# Revit family: Hager-GOLF-Surface_mounted-IP40-With_Cover-With_DIN-Hosted-ES-es
name_source: partatom
category: Electrical Equipment
units: mm (PartAtom-declared; Revit-internal decimal feet)

## family parameters
Cut with Voids When Loaded = No
Host = Face
Maintain Annotation Orientation = Yes
Panel Configuration = Two Columns, Circuits Across
Part Type = Panelboard
Room Calculation Point = No
Round Connector Dimension = Use Diameter
Shared = No

## types (38) — shared parameters
BC_MODEL_ID = 1539134
BC_OBJECT_ID = 512269
BC_OBJECT_VERSION = #5
Code hager = ADD-EC000214_EU
EF000003 - Método de montaje = Montado superficial (escayola)
EF000007 - Color = Blanco
EF000024 - Resistente a UV = No
EF000049 - Profundidad = 99 mm  [stored 0.324803 ft]
EF000116 - Número RAL = 9010
EF000118 - Con placa de montaje = No
EF001062 - Versión de CEM = No
EF001088 - Posibilidad de extensión = Yes
EF001134 - Carril DIN = Yes
EF004462 - Tipo de cierre = Otros
EF005474 - Grado de protección (IP) = IP40
EF006306 - Con candado = No
EF009212 - Versión de la cubierta = Cerrado
EF015941 - Puerta de transmisión de señal = Yes
ETIM class code = EC000214
ETIM class name = Small distribution board
HG000001 - Número de columnas = 1
HG000002-with door or cover-es = Yes
HG000003-Range-es = GOLF
HG000005-Thickness-es = 2 mm  [stored 0.00656168 ft]
HG000006-Flush mounted-es = No
HG000009-Double swing door-es = No
HG000010-Asymmetric doors-es = No
HG000011-Empty rows from bottom-es = No
HG000012-Door swing angle-es = 90.00°
HG000013-Door on the left-es = No
HG000014-Door on the right-es = Yes
HG000015-Clearance visibility-es = Yes
HG000016-Door 3D visibility-es = Yes
HG000017-Distance between poles-es = 18 mm  [stored 0.0590551 ft]
HG000060-RAL-number = 9010
HG000099-Onfly Template ID-es-ES = 507532
Manufacturer = Hager
Name = Hager-GOLF-Surface_mounted-IP40-With_Cover-With_DIN-NoHosted-ES-es
Name BIM&CO = Electricity
Name hager = ADD_Enclosures_EC000214
Uniformat = Low Tension Service & Dist.
Uniformat code = D501001
zero-valued in all types: Default Elevation, EF000218 - Profundidad de instalación, EF000332 - Altura de la instalación, EF000846 - Anchura de montaje, EF001131 - Profundidad interna, HG000007-Number of empty columns-es, HG000008-Number of empty rows-es

## per-type parameters (varying)
| type | BC_VARIANT_ID | EF000008 - Anchura | EF000040 - Altura | EF000266 - Número de filas | EF002950 - Ancho en número de espacios modulares | EF006244 - Tapa/puerta transparente | EF015776 - Borne de tierra | EF015777 - Borne neutro | HG000004-Manufacturer reference-es | HGEF000266-Número de filas | HGEF0002950-Ancho en número de espacios modulares |
| GOLF-Surface_mounted_W138_H184_D99_4_Modular_Spacing-VS104PE | 1169241 | 138 mm  [stored 0.452756 ft] | 184 mm  [stored 0.603675 ft] | 1 | 4 | No | Yes | No | VS104PE | 1 | 4 |
| GOLF-Surface_mounted_W138_H184_D99_4_Modular_Spacing-VS104PEB | 1169246 | 138 mm  [stored 0.452756 ft] | 184 mm  [stored 0.603675 ft] | 1 | 4 | No | No | No | VS104PEB | 1 | 4 |
| GOLF-Surface_mounted_W138_H184_D99_4_Modular_Spacing-VS104TE | 1169249 | 138 mm  [stored 0.452756 ft] | 184 mm  [stored 0.603675 ft] | 1 | 4 | Yes | Yes | No | VS104TE | 1 | 4 |
| GOLF-Surface_mounted_W210_H184_D99_8_Modular_Spacing-VS108PE | 1169253 | 210 mm  [stored 0.688976 ft] | 184 mm  [stored 0.603675 ft] | 1 | 8 | No | Yes | No | VS108PE | 1 | 8 |
| GOLF-Surface_mounted_W210_H184_D99_8_Modular_Spacing-VS108PEB | 1169256 | 210 mm  [stored 0.688976 ft] | 184 mm  [stored 0.603675 ft] | 1 | 8 | No | No | No | VS108PEB | 1 | 8 |
| GOLF-Surface_mounted_W210_H184_D99_8_Modular_Spacing-VS108TE | 1169260 | 210 mm  [stored 0.688976 ft] | 184 mm  [stored 0.603675 ft] | 1 | 8 | Yes | Yes | No | VS108TE | 1 | 8 |
| GOLF-Surface_mounted_W282_H252_D99_12_Modular_Spacing-VS112PE | 1169262 | 282 mm | 252 mm  [stored 0.826772 ft] | 1 | 12 | No | Yes | No | VS112PE | 1 | 12 |
| GOLF-Surface_mounted_W282_H252_D99_12_Modular_Spacing-VS112PEB | 1169265 | 282 mm | 252 mm  [stored 0.826772 ft] | 1 | 12 | No | No | No | VS112PEB | 1 | 12 |
| GOLF-Surface_mounted_W282_H252_D99_12_Modular_Spacing-VS112PY | 1169269 | 282 mm | 252 mm  [stored 0.826772 ft] | 1 | 12 | No | Yes | Yes | VS112PY | 1 | 12 |
| GOLF-Surface_mounted_W282_H252_D99_12_Modular_Spacing-VS112TE | 1169273 | 282 mm | 252 mm  [stored 0.826772 ft] | 1 | 12 | Yes | Yes | No | VS112TE | 1 | 12 |
| GOLF-Surface_mounted_W390_H252_D99_18_Modular_Spacing-VS118PES | 1169276 | 390 mm  [stored 1.27953 ft] | 252 mm  [stored 0.826772 ft] | 1 | 18 | No | No | No | VS118PES | 1 | 18 |
| GOLF-Surface_mounted_W390_H252_D99_18_Modular_Spacing-VS118PY | 1169279 | 390 mm  [stored 1.27953 ft] | 252 mm  [stored 0.826772 ft] | 1 | 18 | No | Yes | Yes | VS118PY | 1 | 18 |
| GOLF-Surface_mounted_W390_H252_D99_18_Modular_Spacing-VS118TES | 1169283 | 390 mm  [stored 1.27953 ft] | 252 mm  [stored 0.826772 ft] | 1 | 18 | Yes | No | No | VS118TES | 1 | 18 |
| GOLF-Surface_mounted_W390_H252_D99_18_Modular_Spacing-VS118TF | 1169287 | 390 mm  [stored 1.27953 ft] | 252 mm  [stored 0.826772 ft] | 1 | 18 | Yes | Yes | No | VS118TF | 1 | 18 |
| GOLF-Surface_mounted_W462_H252_D99_22_Modular_Spacing-VS122PY | 1169290 | 462 mm  [stored 1.51575 ft] | 252 mm  [stored 0.826772 ft] | 1 | 22 | No | Yes | Yes | VS122PY | 1 | 22 |
| GOLF-Surface_mounted_W282_H377_D99_12_Modular_Spacing-VS212PE | 1169294 | 282 mm | 377 mm  [stored 1.23688 ft] | 2 | 12 | No | Yes | No | VS212PE | 2 | 12 |
| GOLF-Surface_mounted_W282_H377_D99_12_Modular_Spacing-VS212PEB | 1169298 | 282 mm | 377 mm  [stored 1.23688 ft] | 2 | 12 | No | No | No | VS212PEB | 2 | 12 |
| GOLF-Surface_mounted_W282_H377_D99_12_Modular_Spacing-VS212PY | 1169301 | 282 mm | 377 mm  [stored 1.23688 ft] | 2 | 12 | No | Yes | Yes | VS212PY | 2 | 12 |
| GOLF-Surface_mounted_W282_H377_D99_12_Modular_Spacing-VS212TE | 1169304 | 282 mm | 377 mm  [stored 1.23688 ft] | 2 | 12 | Yes | Yes | No | VS212TE | 2 | 12 |
| GOLF-Surface_mounted_W282_H377_D99_12_Modular_Spacing-VS212TY | 1169307 | 282 mm | 377 mm  [stored 1.23688 ft] | 2 | 12 | Yes | Yes | Yes | VS212TY | 2 | 12 |
| GOLF-Surface_mounted_W390_H377_D99_18_Modular_Spacing-VS218PES | 1169309 | 390 mm  [stored 1.27953 ft] | 377 mm  [stored 1.23688 ft] | 2 | 18 | No | No | No | VS218PES | 2 | 18 |
| GOLF-Surface_mounted_W390_H377_D99_18_Modular_Spacing-VS218PY | 1169311 | 390 mm  [stored 1.27953 ft] | 377 mm  [stored 1.23688 ft] | 2 | 18 | No | Yes | Yes | VS218PY | 2 | 18 |
| GOLF-Surface_mounted_W390_H377_D99_18_Modular_Spacing-VS218TES | 1169313 | 390 mm  [stored 1.27953 ft] | 377 mm  [stored 1.23688 ft] | 2 | 18 | Yes | No | No | VS218TES | 2 | 18 |
| GOLF-Surface_mounted_W390_H377_D99_18_Modular_Spacing-VS218TY | 1169315 | 390 mm  [stored 1.27953 ft] | 377 mm  [stored 1.23688 ft] | 2 | 18 | Yes | Yes | Yes | VS218TY | 2 | 18 |
| GOLF-Surface_mounted_W282_H500_D99_12_Modular_Spacing-VS312PE | 1169317 | 282 mm | 500 mm  [stored 1.64042 ft] | 3 | 12 | No | Yes | No | VS312PE | 3 | 12 |
| GOLF-Surface_mounted_W282_H500_D99_12_Modular_Spacing-VS312PY | 1169319 | 282 mm | 500 mm  [stored 1.64042 ft] | 3 | 12 | No | Yes | Yes | VS312PY | 3 | 12 |
| GOLF-Surface_mounted_W282_H500_D99_12_Modular_Spacing-VS312TE | 1169321 | 282 mm | 500 mm  [stored 1.64042 ft] | 3 | 12 | Yes | Yes | No | VS312TE | 3 | 12 |
| GOLF-Surface_mounted_W390_H500_D99_18_Modular_Spacing-VS318PES | 1169323 | 390 mm  [stored 1.27953 ft] | 500 mm  [stored 1.64042 ft] | 3 | 18 | No | No | No | VS318PES | 3 | 18 |
| GOLF-Surface_mounted_W390_H500_D99_18_Modular_Spacing-VS318PY | 1169325 | 390 mm  [stored 1.27953 ft] | 500 mm  [stored 1.64042 ft] | 3 | 18 | No | Yes | Yes | VS318PY | 3 | 18 |
| GOLF-Surface_mounted_W390_H500_D99_18_Modular_Spacing-VS318TES | 1169327 | 390 mm  [stored 1.27953 ft] | 500 mm  [stored 1.64042 ft] | 3 | 18 | Yes | No | No | VS318TES | 3 | 18 |
| GOLF-Surface_mounted_W282_H647_D99_12_Modular_Spacing-VS412PE | 1169329 | 282 mm | 647 mm  [stored 2.1227 ft] | 4 | 12 | No | Yes | No | VS412PE | 4 | 12 |
| GOLF-Surface_mounted_W282_H647_D99_12_Modular_Spacing-VS412PY | 1169331 | 282 mm | 647 mm  [stored 2.1227 ft] | 4 | 12 | No | Yes | Yes | VS412PY | 4 | 12 |
| GOLF-Surface_mounted_W282_H647_D99_12_Modular_Spacing-VS412TE | 1169334 | 282 mm | 647 mm  [stored 2.1227 ft] | 4 | 12 | Yes | Yes | No | VS412TE | 4 | 12 |
| GOLF-Surface_mounted_W390_H647_D99_18_Modular_Spacing-VS418PES | 1169336 | 390 mm  [stored 1.27953 ft] | 647 mm  [stored 2.1227 ft] | 4 | 18 | No | No | No | VS418PES | 4 | 18 |
| GOLF-Surface_mounted_W390_H647_D99_18_Modular_Spacing-VS418PF | 1169338 | 390 mm  [stored 1.27953 ft] | 647 mm  [stored 2.1227 ft] | 4 | 18 | No | Yes | No | VS418PF | 4 | 18 |
| GOLF-Surface_mounted_W390_H647_D99_18_Modular_Spacing-VS418PY | 1169340 | 390 mm  [stored 1.27953 ft] | 647 mm  [stored 2.1227 ft] | 4 | 18 | No | Yes | Yes | VS418PY | 4 | 18 |
| GOLF-Surface_mounted_W390_H647_D99_18_Modular_Spacing-VS418TES | 1169343 | 390 mm  [stored 1.27953 ft] | 647 mm  [stored 2.1227 ft] | 4 | 18 | Yes | No | No | VS418TES | 4 | 18 |
| GOLF-Surface_mounted_W390_H647_D99_18_Modular_Spacing-VS418TY | 1169345 | 390 mm  [stored 1.27953 ft] | 647 mm  [stored 2.1227 ft] | 4 | 18 | Yes | Yes | Yes | VS418TY | 4 | 18 |

note: column(s) folded — value = type name in every type: Reference

note: [stored X ft] marks values corroborated as IEEE doubles in the binary element streams (Revit-internal decimal feet)

## geometry (parser evidence)
native form markers: Sweep x14
no freeform markers — native parametric forms only
